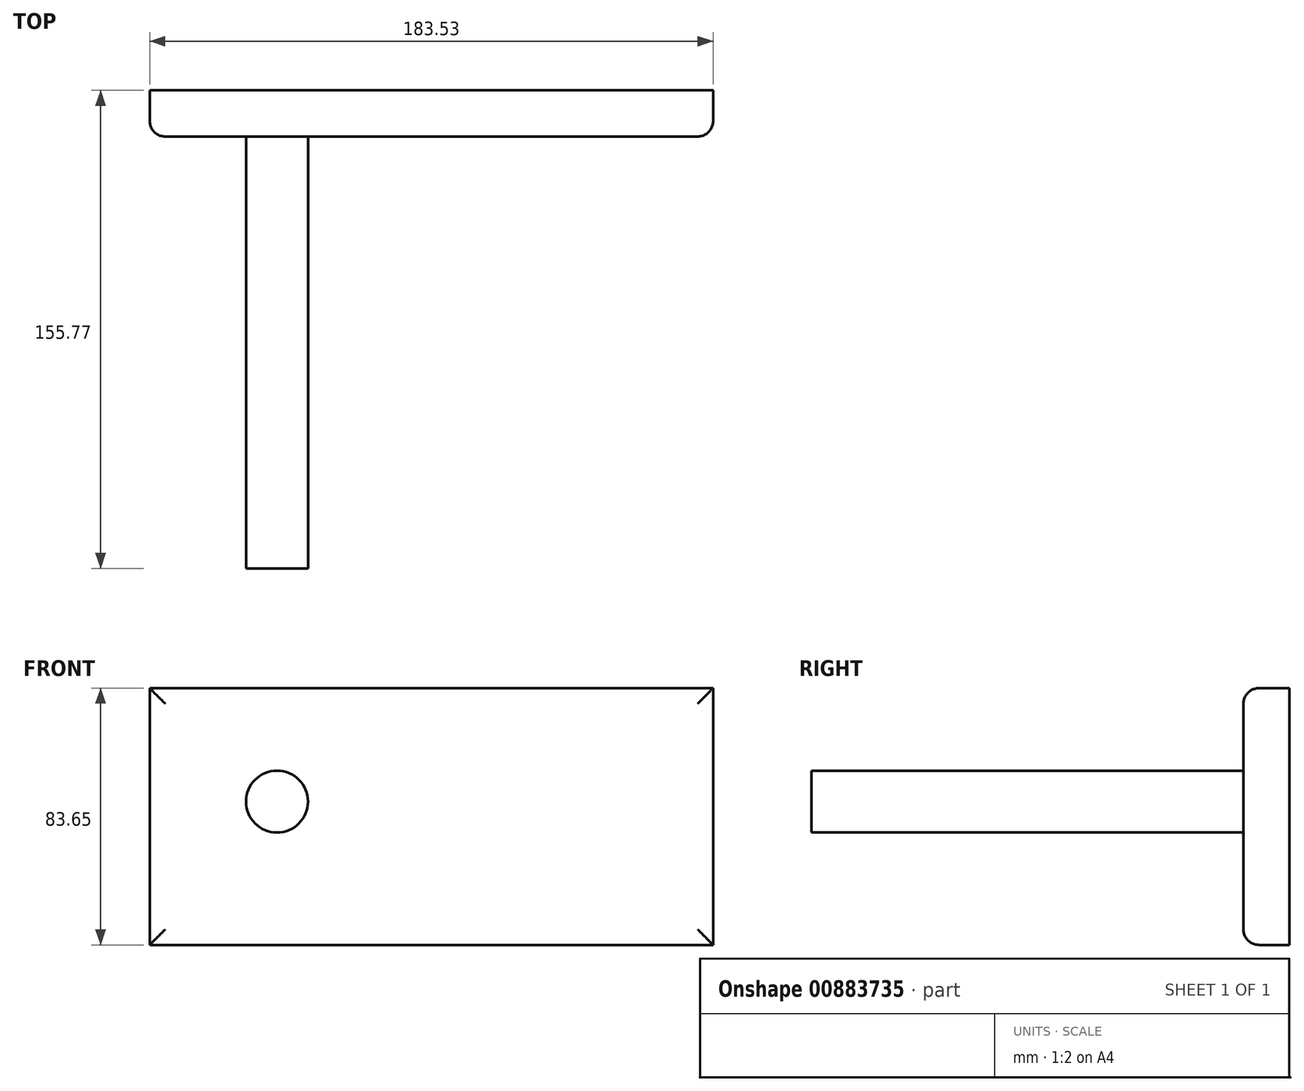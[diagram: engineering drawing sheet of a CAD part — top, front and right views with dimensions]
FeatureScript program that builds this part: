
annotation { "Feature Type Name" : "Feature", "Feature Type Description" : "" }
export const myFeature = defineFeature(function(context is Context, id is Id, definition is map)
    precondition{}
    {
        {
            var Q0;
            Q0=qCreatedBy(makeId("Front.planeOp"),FACE);
            var sketch = newSketch(context, id + "F0", { "sketchPlane" : qUnion([Q0])});
            skLineSegment(sketch, "E0.bottom", {"start": v(92.37, 83.65) * mm, "end": v(-91.16, 83.65) * mm});
            skLineSegment(sketch, "E0.top", {"start": v(92.37, 0) * mm, "end": v(-91.16, 0) * mm});
            skLineSegment(sketch, "E0.left", {"start": v(92.37, 83.65) * mm, "end": v(92.37, 0) * mm});
            skLineSegment(sketch, "E0.right", {"start": v(-91.16, 83.65) * mm, "end": v(-91.16, 0) * mm});
            skSolve(sketch);
        }
        {
            var Q0;
            Q0 = qSketchRegion(id + "F0", true);
            extrude(context, id + "F1", {"entities" : qUnion([Q0]), "depth" : 15.06 * mm, "offsetDistance" : 25.4 * mm});
        }
        {
            var Q0;
            Q0=makeQuery(id+"F1.opExtrude","CAP_EDGE",EDGE,{"disambiguationData":[OSD([sQuery(id+"F0.wireOp",EDGE,"E0.bottom")])],"isStart":false});
            var Q1;
            Q1=makeQuery(id+"F1.opExtrude","CAP_EDGE",EDGE,{"disambiguationData":[OSD([sQuery(id+"F0.wireOp",EDGE,"E0.right")])],"isStart":false});
            var Q2;
            Q2=makeQuery(id+"F1.opExtrude","CAP_EDGE",EDGE,{"disambiguationData":[OSD([sQuery(id+"F0.wireOp",EDGE,"E0.left")])],"isStart":false});
            var Q3;
            Q3=makeQuery(id+"F1.opExtrude","CAP_EDGE",EDGE,{"disambiguationData":[OSD([sQuery(id+"F0.wireOp",EDGE,"E0.top")])],"isStart":false});
            fillet(context, id + "F2", {"entities" : qUnion([Q0, Q1, Q2, Q3]), "radius" : 5.08 * mm, "tangentPropagation" : true, "allowEdgeOverflow" : false});
        }
        {
            var Q0;
            Q0=makeQuery(id+"F1.opExtrude","CAP_FACE",FACE,{"disambiguationData":[OSD([sQuery(id+"F0.wireOp",EDGE,"E0.bottom"),sQuery(id+"F0.wireOp",EDGE,"E0.top"),sQuery(id+"F0.wireOp",EDGE,"E0.left"),sQuery(id+"F0.wireOp",EDGE,"E0.right")])],"isStart":false});
            var sketch = newSketch(context, id + "F3", { "sketchPlane" : qUnion([Q0])});
            skCircle(sketch, "E1", {"center": v(-49.69, 46.7) * mm, "radius": 10.08 * mm});
            skSolve(sketch);
        }
        {
            var Q0;
            Q0 = qSketchRegion(id + "F3", true);
            extrude(context, id + "F4", {"entities" : qUnion([Q0]), "operationType" : NewBodyOperationType.ADD, "depth" : 140.71 * mm, "offsetDistance" : 25.4 * mm});
        }
    });
